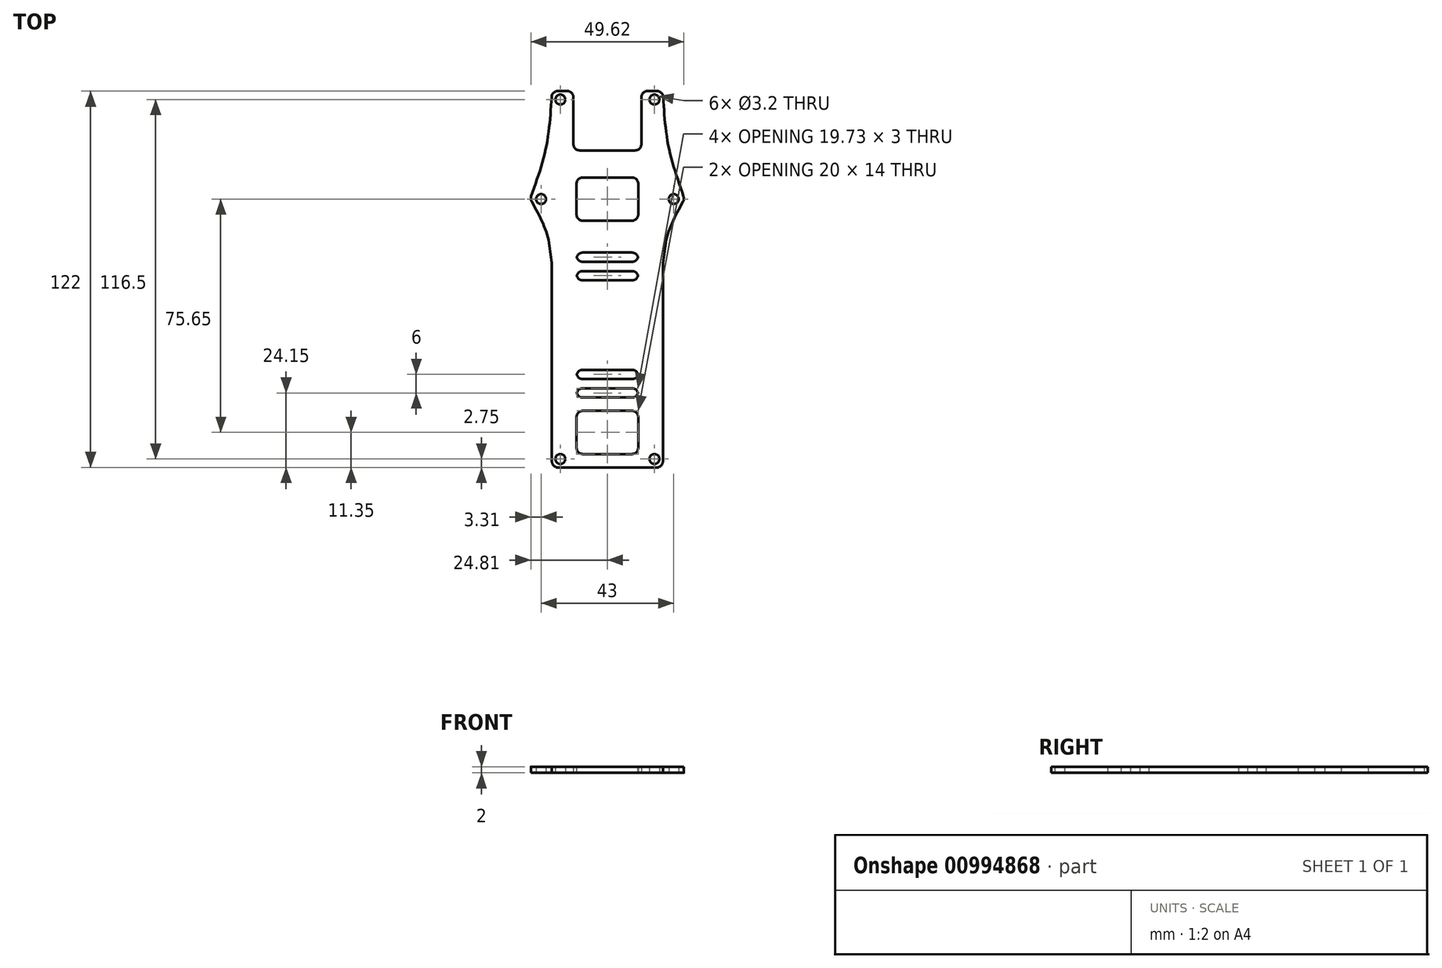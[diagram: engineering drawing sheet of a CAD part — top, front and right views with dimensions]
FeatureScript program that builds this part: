
annotation { "Feature Type Name" : "Feature", "Feature Type Description" : "" }
export const myFeature = defineFeature(function(context is Context, id is Id, definition is map)
    precondition{}
    {
        {
            var Q0;
            Q0=qCreatedBy(makeId("Top.planeOp"),FACE);
            var sketch = newSketch(context, id + "F0", { "sketchPlane" : qUnion([Q0])});
            skLineSegment(sketch, "E0.bottom", {"start": v(-18, 72) * mm, "end": v(-11, 72) * mm});
            skLineSegment(sketch, "E0.left", {"start": v(-18, 72) * mm, "end": v(-18, 0) * mm});
            skLineSegment(sketch, "E0.right", {"start": v(18, 72) * mm, "end": v(18, 0) * mm});
            skPoint(sketch, "E0.middle", {"position": v(0, 0) * mm});
            skLineSegment(sketch, "E1", {"start": v(0, 0) * mm, "end": v(15.25, 0) * mm, "construction": true});
            skCircle(sketch, "E2", {"center": v(15.25, 15.25) * mm, "radius": 1.6 * mm, "construction": true});
            skCircle(sketch, "E3.MirrorC", {"center": v(15.25, -15.25) * mm, "radius": 1.6 * mm, "construction": true});
            skCircle(sketch, "E4.MirrorC", {"center": v(-15.25, -15.25) * mm, "radius": 1.6 * mm, "construction": true});
            skCircle(sketch, "E5.MirrorC", {"center": v(-15.25, 15.25) * mm, "radius": 1.6 * mm, "construction": true});
            skCircle(sketch, "E6.MirrorC", {"center": v(15.25, -47.25) * mm, "radius": 1.6 * mm});
            skCircle(sketch, "E7.MirrorC", {"center": v(-15.25, -47.25) * mm, "radius": 1.6 * mm});
            skCircle(sketch, "E8", {"center": v(21.5, 37) * mm, "radius": 1.6 * mm});
            skCircle(sketch, "E9.MirrorC", {"center": v(-21.5, 37) * mm, "radius": 1.6 * mm});
            skCircle(sketch, "E10", {"center": v(21.5, 37) * mm, "radius": 2.5 * mm, "construction": true});
            skCircle(sketch, "E11", {"center": v(15.25, 69.25) * mm, "radius": 1.6 * mm});
            skCircle(sketch, "E12.MirrorC", {"center": v(-15.25, 69.25) * mm, "radius": 1.6 * mm});
            skLineSegment(sketch, "E13.bottom", {"start": v(11, 52.77) * mm, "end": v(-11, 52.77) * mm});
            skLineSegment(sketch, "E13.left", {"start": v(11, 52.77) * mm, "end": v(11, 72) * mm});
            skLineSegment(sketch, "E13.right", {"start": v(-11, 52.77) * mm, "end": v(-11, 72) * mm});
            skPoint(sketch, "E13.middle", {"position": v(0, 72) * mm});
            skLineSegment(sketch, "E14.trimOffspring", {"start": v(11, 72) * mm, "end": v(18, 72) * mm});
            skLineSegment(sketch, "E15", {"start": v(-15.25, 15.25) * mm, "end": v(-15.25, 13.65) * mm, "construction": true});
            skLineSegment(sketch, "E16", {"start": v(-15.25, 13.65) * mm, "end": v(15.25, 13.65) * mm, "construction": true});
            skLineSegment(sketch, "E17", {"start": v(0, 13.65) * mm, "end": v(0, 10.65) * mm, "construction": true});
            skLineSegment(sketch, "E18.bottom", {"start": v(10, 10.65) * mm, "end": v(-10, 10.65) * mm});
            skLineSegment(sketch, "E18.top", {"start": v(10, 13.65) * mm, "end": v(-10, 13.65) * mm});
            skLineSegment(sketch, "E18.left", {"start": v(10, 10.65) * mm, "end": v(10, 13.65) * mm});
            skLineSegment(sketch, "E18.right", {"start": v(-10, 10.65) * mm, "end": v(-10, 13.65) * mm});
            skPoint(sketch, "E18.middle", {"position": v(0, 12.15) * mm});
            skLineSegment(sketch, "E19", {"start": v(0, -24.35) * mm, "end": v(0, -27.35) * mm, "construction": true});
            skLineSegment(sketch, "E20.bottom", {"start": v(10, -24.35) * mm, "end": v(-10, -24.35) * mm});
            skLineSegment(sketch, "E20.top", {"start": v(10, -27.35) * mm, "end": v(-10, -27.35) * mm});
            skLineSegment(sketch, "E20.left", {"start": v(10, -24.35) * mm, "end": v(10, -27.35) * mm});
            skLineSegment(sketch, "E20.right", {"start": v(-10, -24.35) * mm, "end": v(-10, -27.35) * mm});
            skPoint(sketch, "E20.middle", {"position": v(0, -25.85) * mm});
            skLineSegment(sketch, "E21.bottom", {"start": v(-18, 0) * mm, "end": v(18, 0) * mm});
            skLineSegment(sketch, "E22.top", {"start": v(-18, -50) * mm, "end": v(18, -50) * mm});
            skLineSegment(sketch, "E22.left", {"start": v(-18, 0) * mm, "end": v(-18, -50) * mm});
            skLineSegment(sketch, "E22.right", {"start": v(18, 0) * mm, "end": v(18, -50) * mm});
            skLineSegment(sketch, "E23", {"start": v(0, -50) * mm, "end": v(0, -45.65) * mm, "construction": true});
            skLineSegment(sketch, "E24", {"start": v(0, -45.65) * mm, "end": v(10, -45.65) * mm});
            skLineSegment(sketch, "E25", {"start": v(10, -31.65) * mm, "end": v(10, -45.65) * mm});
            skLineSegment(sketch, "E26", {"start": v(10, -31.65) * mm, "end": v(0, -31.65) * mm});
            skLineSegment(sketch, "E27", {"start": v(0, -31.65) * mm, "end": v(-10, -31.65) * mm});
            skLineSegment(sketch, "E28", {"start": v(-10, -31.65) * mm, "end": v(-10, -45.65) * mm});
            skLineSegment(sketch, "E29", {"start": v(-10, -45.65) * mm, "end": v(0, -45.65) * mm});
            skLineSegment(sketch, "E30.MirrorCS", {"start": v(-25, 37) * mm, "end": v(-18, 15.25) * mm, "construction": true});
            skLineSegment(sketch, "E31", {"start": v(18, 72) * mm, "end": v(25, 37) * mm, "construction": true});
            skLineSegment(sketch, "E32", {"start": v(21.5, 54.5) * mm, "end": v(18, 54.5) * mm, "construction": true});
            skFitSpline(sketch, "E33", {"points": [v(18, 72) * mm, v(19.75, 54.5) * mm, v(25, 37) * mm], "startDerivative": vector(1.83, -35.5) * mm, "endDerivative": vector(12.13, -34.5) * mm});
            skFitSpline(sketch, "E34.MirrorCS", {"points": [v(-18, 72) * mm, v(-19.75, 54.5) * mm, v(-25, 37) * mm], "startDerivative": vector(-1.83, -35.5) * mm, "endDerivative": vector(-12.13, -34.5) * mm});
            skLineSegment(sketch, "E35", {"start": v(-21.5, 26.13) * mm, "end": v(-18, 26.13) * mm, "construction": true});
            skFitSpline(sketch, "E36", {"points": [v(-25, 37) * mm, v(-19.75, 26.13) * mm, v(-18, 15.25) * mm], "startDerivative": vector(11.97, -21) * mm, "endDerivative": vector(1.95, -22.5) * mm});
            skFitSpline(sketch, "E37.MirrorCS", {"points": [v(25, 37) * mm, v(19.75, 26.13) * mm, v(18, 15.25) * mm], "startDerivative": vector(-11.97, -21) * mm, "endDerivative": vector(-1.95, -22.5) * mm});
            skLineSegment(sketch, "E38.bottom", {"start": v(10, 19.65) * mm, "end": v(-10, 19.65) * mm});
            skLineSegment(sketch, "E38.top", {"start": v(10, 16.65) * mm, "end": v(-10, 16.65) * mm});
            skLineSegment(sketch, "E38.left", {"start": v(10, 19.65) * mm, "end": v(10, 16.65) * mm});
            skLineSegment(sketch, "E38.right", {"start": v(-10, 19.65) * mm, "end": v(-10, 16.65) * mm});
            skPoint(sketch, "E38.middle", {"position": v(0, 18.15) * mm});
            skLineSegment(sketch, "E39.bottom", {"start": v(10, -21.35) * mm, "end": v(-10, -21.35) * mm});
            skLineSegment(sketch, "E39.top", {"start": v(10, -18.35) * mm, "end": v(-10, -18.35) * mm});
            skLineSegment(sketch, "E39.left", {"start": v(10, -21.35) * mm, "end": v(10, -18.35) * mm});
            skLineSegment(sketch, "E39.right", {"start": v(-10, -21.35) * mm, "end": v(-10, -18.35) * mm});
            skPoint(sketch, "E39.middle", {"position": v(0, -19.85) * mm});
            skLineSegment(sketch, "E40", {"start": v(-10, -45.65) * mm, "end": v(-15.25, -45.65) * mm, "construction": true});
            skLineSegment(sketch, "E41.bottom", {"start": v(10, 44) * mm, "end": v(-10, 44) * mm});
            skLineSegment(sketch, "E41.top", {"start": v(10, 30) * mm, "end": v(-10, 30) * mm});
            skLineSegment(sketch, "E41.left", {"start": v(10, 44) * mm, "end": v(10, 30) * mm});
            skLineSegment(sketch, "E41.right", {"start": v(-10, 44) * mm, "end": v(-10, 30) * mm});
            skPoint(sketch, "E41.middle", {"position": v(0, 37) * mm});
            skLineSegment(sketch, "E42", {"start": v(0, 37) * mm, "end": v(-21.5, 37) * mm, "construction": true});
            skSolve(sketch);
        }
        {
            var Q0;
            Q0=qSketchRegion(id+"F0",true);
            extrude(context, id + "F1", {"entities" : qUnion([Q0]), "depth" : 2 * mm, "offsetDistance" : 25 * mm});
        }
        {
            var Q0;
            Q0=makeQuery(id+"F1.opExtrude","SWEPT_EDGE",EDGE,{"disambiguationData":[OSD([sQuery(id+"F0.wireOp",EDGE,"E13.bottom"),sQuery(id+"F0.wireOp",EDGE,"E13.right")])]});
            var Q1;
            Q1=makeQuery(id+"F1.opExtrude","SWEPT_EDGE",EDGE,{"disambiguationData":[OSD([sQuery(id+"F0.wireOp",EDGE,"E13.bottom"),sQuery(id+"F0.wireOp",EDGE,"E13.left")])]});
            var Q2;
            Q2=makeQuery(id+"F1.opExtrude","SWEPT_EDGE",EDGE,{"disambiguationData":[OSD([sQuery(id+"F0.wireOp",EDGE,"E13.left"),sQuery(id+"F0.wireOp",EDGE,"E14.trimOffspring")])]});
            var Q3;
            Q3=makeQuery(id+"F1.opExtrude","SWEPT_EDGE",EDGE,{"disambiguationData":[OSD([sQuery(id+"F0.wireOp",EDGE,"E0.bottom"),sQuery(id+"F0.wireOp",EDGE,"E13.right")])]});
            var Q4;
            Q4=makeQuery(id+"F1.opExtrude","SWEPT_EDGE",EDGE,{"disambiguationData":[OSD([sQuery(id+"F0.wireOp",EDGE,"E0.bottom"),sQuery(id+"F0.wireOp",EDGE,"E0.left")])]});
            var Q5;
            Q5=makeQuery(id+"F1.opExtrude","SWEPT_EDGE",EDGE,{"disambiguationData":[OSD([sQuery(id+"F0.wireOp",EDGE,"E0.right"),sQuery(id+"F0.wireOp",EDGE,"E14.trimOffspring")])]});
            var Q6;
            Q6=makeQuery(id+"F1.opExtrude","SWEPT_EDGE",EDGE,{"disambiguationData":[OSD([sQuery(id+"F0.wireOp",EDGE,"E0.top"),sQuery(id+"F0.wireOp",EDGE,"E0.right")])]});
            var Q7;
            Q7=makeQuery(id+"F1.opExtrude","SWEPT_EDGE",EDGE,{"disambiguationData":[OSD([sQuery(id+"F0.wireOp",EDGE,"E0.top"),sQuery(id+"F0.wireOp",EDGE,"E0.left")])]});
            var Q8;
            Q8=makeQuery(id+"F1.opExtrude","SWEPT_EDGE",EDGE,{"disambiguationData":[OSD([sQuery(id+"F0.wireOp",EDGE,"E18.top"),sQuery(id+"F0.wireOp",EDGE,"E18.left")])]});
            var Q9;
            Q9=makeQuery(id+"F1.opExtrude","SWEPT_EDGE",EDGE,{"disambiguationData":[OSD([sQuery(id+"F0.wireOp",EDGE,"E18.top"),sQuery(id+"F0.wireOp",EDGE,"E18.right")])]});
            var Q10;
            Q10=makeQuery(id+"F1.opExtrude","SWEPT_EDGE",EDGE,{"disambiguationData":[OSD([sQuery(id+"F0.wireOp",EDGE,"E18.bottom"),sQuery(id+"F0.wireOp",EDGE,"E18.right")])]});
            var Q11;
            Q11=makeQuery(id+"F1.opExtrude","SWEPT_EDGE",EDGE,{"disambiguationData":[OSD([sQuery(id+"F0.wireOp",EDGE,"E18.bottom"),sQuery(id+"F0.wireOp",EDGE,"E18.left")])]});
            var Q12;
            Q12=makeQuery(id+"F1.opExtrude","SWEPT_EDGE",EDGE,{"disambiguationData":[OSD([sQuery(id+"F0.wireOp",EDGE,"E20.bottom"),sQuery(id+"F0.wireOp",EDGE,"E20.left")])]});
            var Q13;
            Q13=makeQuery(id+"F1.opExtrude","SWEPT_EDGE",EDGE,{"disambiguationData":[OSD([sQuery(id+"F0.wireOp",EDGE,"E20.bottom"),sQuery(id+"F0.wireOp",EDGE,"E20.right")])]});
            var Q14;
            Q14=makeQuery(id+"F1.opExtrude","SWEPT_EDGE",EDGE,{"disambiguationData":[OSD([sQuery(id+"F0.wireOp",EDGE,"E20.top"),sQuery(id+"F0.wireOp",EDGE,"E20.right")])]});
            var Q15;
            Q15=makeQuery(id+"F1.opExtrude","SWEPT_EDGE",EDGE,{"disambiguationData":[OSD([sQuery(id+"F0.wireOp",EDGE,"E20.top"),sQuery(id+"F0.wireOp",EDGE,"E20.left")])]});
            var Q16;
            Q16=makeQuery(id+"F1.opExtrude","SWEPT_EDGE",EDGE,{"disambiguationData":[OSD([sQuery(id+"F0.wireOp",EDGE,"E22.top"),sQuery(id+"F0.wireOp",EDGE,"E22.left")])]});
            var Q17;
            Q17=makeQuery(id+"F1.opExtrude","SWEPT_EDGE",EDGE,{"disambiguationData":[OSD([sQuery(id+"F0.wireOp",EDGE,"E22.top"),sQuery(id+"F0.wireOp",EDGE,"E22.right")])]});
            var Q18;
            Q18=makeQuery(id+"F1.opExtrude","SWEPT_EDGE",EDGE,{"disambiguationData":[OSD([sQuery(id+"F0.wireOp",EDGE,"E27"),sQuery(id+"F0.wireOp",EDGE,"E28")])]});
            var Q19;
            Q19=makeQuery(id+"F1.opExtrude","SWEPT_EDGE",EDGE,{"disambiguationData":[OSD([sQuery(id+"F0.wireOp",EDGE,"E25"),sQuery(id+"F0.wireOp",EDGE,"E26")])]});
            var Q20;
            Q20=makeQuery(id+"F1.opExtrude","SWEPT_EDGE",EDGE,{"disambiguationData":[OSD([sQuery(id+"F0.wireOp",EDGE,"E24"),sQuery(id+"F0.wireOp",EDGE,"E25")])]});
            var Q21;
            Q21=makeQuery(id+"F1.opExtrude","SWEPT_EDGE",EDGE,{"disambiguationData":[OSD([sQuery(id+"F0.wireOp",EDGE,"E28"),sQuery(id+"F0.wireOp",EDGE,"E29")])]});
            var Q22;
            Q22=makeQuery(id+"F1.opExtrude","SWEPT_EDGE",EDGE,{"disambiguationData":[OSD([sQuery(id+"F0.wireOp",EDGE,"7ddf48ca-3a1b-4fe8-b939-8c2d3d607d9d0.MirrorCS"),sQuery(id+"F0.wireOp",EDGE,"E30.MirrorCS")])]});
            var Q23;
            Q23=makeQuery(id+"F1.opExtrude","SWEPT_EDGE",EDGE,{"disambiguationData":[OSD([sQuery(id+"F0.wireOp",EDGE,"79cEYJIF-AjxS-aiUu-jvyM-gJTKuYMF5cMQ"),sQuery(id+"F0.wireOp",EDGE,"uUAegvua-vEfk-1mnY-6KAw-FU2lr9x1sRSC")])]});
            var Q24;
            Q24=makeQuery(id+"F1.opExtrude","SWEPT_EDGE",EDGE,{"disambiguationData":[OSD([sQuery(id+"F0.wireOp",EDGE,"E34.MirrorCS"),sQuery(id+"F0.wireOp",EDGE,"E36")])]});
            var Q25;
            Q25=makeQuery(id+"F1.opExtrude","SWEPT_EDGE",EDGE,{"disambiguationData":[OSD([sQuery(id+"F0.wireOp",EDGE,"E33"),sQuery(id+"F0.wireOp",EDGE,"E37.MirrorCS")])]});
            var Q26;
            Q26=makeQuery(id+"F1.opExtrude","SWEPT_EDGE",EDGE,{"disambiguationData":[OSD([sQuery(id+"F0.wireOp",EDGE,"E38.bottom"),sQuery(id+"F0.wireOp",EDGE,"E38.right")])]});
            var Q27;
            Q27=makeQuery(id+"F1.opExtrude","SWEPT_EDGE",EDGE,{"disambiguationData":[OSD([sQuery(id+"F0.wireOp",EDGE,"E38.top"),sQuery(id+"F0.wireOp",EDGE,"E38.right")])]});
            var Q28;
            Q28=makeQuery(id+"F1.opExtrude","SWEPT_EDGE",EDGE,{"disambiguationData":[OSD([sQuery(id+"F0.wireOp",EDGE,"E39.bottom"),sQuery(id+"F0.wireOp",EDGE,"E39.right")])]});
            var Q29;
            Q29=makeQuery(id+"F1.opExtrude","SWEPT_EDGE",EDGE,{"disambiguationData":[OSD([sQuery(id+"F0.wireOp",EDGE,"E39.top"),sQuery(id+"F0.wireOp",EDGE,"E39.right")])]});
            var Q30;
            Q30=makeQuery(id+"F1.opExtrude","SWEPT_EDGE",EDGE,{"disambiguationData":[OSD([sQuery(id+"F0.wireOp",EDGE,"E39.top"),sQuery(id+"F0.wireOp",EDGE,"E39.left")])]});
            var Q31;
            Q31=makeQuery(id+"F1.opExtrude","SWEPT_EDGE",EDGE,{"disambiguationData":[OSD([sQuery(id+"F0.wireOp",EDGE,"E39.bottom"),sQuery(id+"F0.wireOp",EDGE,"E39.left")])]});
            var Q32;
            Q32=makeQuery(id+"F1.opExtrude","SWEPT_EDGE",EDGE,{"disambiguationData":[OSD([sQuery(id+"F0.wireOp",EDGE,"E38.top"),sQuery(id+"F0.wireOp",EDGE,"E38.left")])]});
            var Q33;
            Q33=makeQuery(id+"F1.opExtrude","SWEPT_EDGE",EDGE,{"disambiguationData":[OSD([sQuery(id+"F0.wireOp",EDGE,"E38.bottom"),sQuery(id+"F0.wireOp",EDGE,"E38.left")])]});
            var Q34;
            Q34=makeQuery(id+"F1.opExtrude","SWEPT_EDGE",EDGE,{"disambiguationData":[OSD([sQuery(id+"F0.wireOp",EDGE,"E41.bottom"),sQuery(id+"F0.wireOp",EDGE,"E41.right")])]});
            var Q35;
            Q35=makeQuery(id+"F1.opExtrude","SWEPT_EDGE",EDGE,{"disambiguationData":[OSD([sQuery(id+"F0.wireOp",EDGE,"E41.bottom"),sQuery(id+"F0.wireOp",EDGE,"E41.left")])]});
            var Q36;
            Q36=makeQuery(id+"F1.opExtrude","SWEPT_EDGE",EDGE,{"disambiguationData":[OSD([sQuery(id+"F0.wireOp",EDGE,"E41.top"),sQuery(id+"F0.wireOp",EDGE,"E41.left")])]});
            var Q37;
            Q37=makeQuery(id+"F1.opExtrude","SWEPT_EDGE",EDGE,{"disambiguationData":[OSD([sQuery(id+"F0.wireOp",EDGE,"E41.top"),sQuery(id+"F0.wireOp",EDGE,"E41.right")])]});
            fillet(context, id + "F2", {"entities" : qUnion([Q0, Q1, Q2, Q3, Q4, Q5, Q6, Q7, Q8, Q9, Q10, Q11, Q12, Q13, Q14, Q15, Q16, Q17, Q18, Q19, Q20, Q21, Q22, Q23, Q24, Q25, Q26, Q27, Q28, Q29, Q30, Q31, Q32, Q33, Q34, Q35, Q36, Q37]), "radius" : 2 * mm, "tangentPropagation" : true, "defaultsChanged" : false, "vertexSettings" : [], "allowEdgeOverflow" : false});
        }
        {
            var Q0;
            {var subQ0=sQuery(id+"F0.wireOp",EDGE,"E20.right");Q0=makeQuery(id+"F2.opFillet","BLEND_EDGE",EDGE,{"blendedFrom":[makeQuery(id+"F1.opExtrude","SWEPT_EDGE",EDGE,{"disambiguationData":[OSD([sQuery(id+"F0.wireOp",EDGE,"E20.bottom"),subQ0])]}),makeQuery(id+"F1.opExtrude","SWEPT_EDGE",EDGE,{"disambiguationData":[OSD([sQuery(id+"F0.wireOp",EDGE,"E20.top"),subQ0])]})],"blendedInto":[]});}
            var Q1;
            {var subQ0=sQuery(id+"F0.wireOp",EDGE,"E20.left");Q1=makeQuery(id+"F2.opFillet","BLEND_EDGE",EDGE,{"blendedFrom":[makeQuery(id+"F1.opExtrude","SWEPT_EDGE",EDGE,{"disambiguationData":[OSD([sQuery(id+"F0.wireOp",EDGE,"E20.bottom"),subQ0])]}),makeQuery(id+"F1.opExtrude","SWEPT_EDGE",EDGE,{"disambiguationData":[OSD([sQuery(id+"F0.wireOp",EDGE,"E20.top"),subQ0])]})],"blendedInto":[]});}
            var Q2;
            {var subQ0=sQuery(id+"F0.wireOp",EDGE,"E18.left");Q2=makeQuery(id+"F2.opFillet","BLEND_EDGE",EDGE,{"blendedFrom":[makeQuery(id+"F1.opExtrude","SWEPT_EDGE",EDGE,{"disambiguationData":[OSD([sQuery(id+"F0.wireOp",EDGE,"E18.bottom"),subQ0])]}),makeQuery(id+"F1.opExtrude","SWEPT_EDGE",EDGE,{"disambiguationData":[OSD([sQuery(id+"F0.wireOp",EDGE,"E18.top"),subQ0])]})],"blendedInto":[]});}
            var Q3;
            {var subQ0=sQuery(id+"F0.wireOp",EDGE,"E18.right");Q3=makeQuery(id+"F2.opFillet","BLEND_EDGE",EDGE,{"blendedFrom":[makeQuery(id+"F1.opExtrude","SWEPT_EDGE",EDGE,{"disambiguationData":[OSD([sQuery(id+"F0.wireOp",EDGE,"E18.bottom"),subQ0])]}),makeQuery(id+"F1.opExtrude","SWEPT_EDGE",EDGE,{"disambiguationData":[OSD([sQuery(id+"F0.wireOp",EDGE,"E18.top"),subQ0])]})],"blendedInto":[]});}
            var Q4;
            {var subQ0=sQuery(id+"F0.wireOp",EDGE,"E38.left");Q4=makeQuery(id+"F2.opFillet","BLEND_EDGE",EDGE,{"blendedFrom":[makeQuery(id+"F1.opExtrude","SWEPT_EDGE",EDGE,{"disambiguationData":[OSD([sQuery(id+"F0.wireOp",EDGE,"E38.bottom"),subQ0])]}),makeQuery(id+"F1.opExtrude","SWEPT_EDGE",EDGE,{"disambiguationData":[OSD([sQuery(id+"F0.wireOp",EDGE,"E38.top"),subQ0])]})],"blendedInto":[]});}
            var Q5;
            {var subQ0=sQuery(id+"F0.wireOp",EDGE,"E38.right");Q5=makeQuery(id+"F2.opFillet","BLEND_EDGE",EDGE,{"blendedFrom":[makeQuery(id+"F1.opExtrude","SWEPT_EDGE",EDGE,{"disambiguationData":[OSD([sQuery(id+"F0.wireOp",EDGE,"E38.bottom"),subQ0])]}),makeQuery(id+"F1.opExtrude","SWEPT_EDGE",EDGE,{"disambiguationData":[OSD([sQuery(id+"F0.wireOp",EDGE,"E38.top"),subQ0])]})],"blendedInto":[]});}
            var Q6;
            {var subQ0=sQuery(id+"F0.wireOp",EDGE,"E39.right");Q6=makeQuery(id+"F2.opFillet","BLEND_EDGE",EDGE,{"blendedFrom":[makeQuery(id+"F1.opExtrude","SWEPT_EDGE",EDGE,{"disambiguationData":[OSD([sQuery(id+"F0.wireOp",EDGE,"E39.bottom"),subQ0])]}),makeQuery(id+"F1.opExtrude","SWEPT_EDGE",EDGE,{"disambiguationData":[OSD([sQuery(id+"F0.wireOp",EDGE,"E39.top"),subQ0])]})],"blendedInto":[]});}
            var Q7;
            {var subQ0=sQuery(id+"F0.wireOp",EDGE,"E39.left");Q7=makeQuery(id+"F2.opFillet","BLEND_EDGE",EDGE,{"blendedFrom":[makeQuery(id+"F1.opExtrude","SWEPT_EDGE",EDGE,{"disambiguationData":[OSD([sQuery(id+"F0.wireOp",EDGE,"E39.bottom"),subQ0])]}),makeQuery(id+"F1.opExtrude","SWEPT_EDGE",EDGE,{"disambiguationData":[OSD([sQuery(id+"F0.wireOp",EDGE,"E39.top"),subQ0])]})],"blendedInto":[]});}
            fillet(context, id + "F3", {"entities" : qUnion([Q0, Q1, Q2, Q3, Q4, Q5, Q6, Q7]), "radius" : 1 * mm, "tangentPropagation" : true, "defaultsChanged" : false, "vertexSettings" : [], "allowEdgeOverflow" : false});
        }
    });
